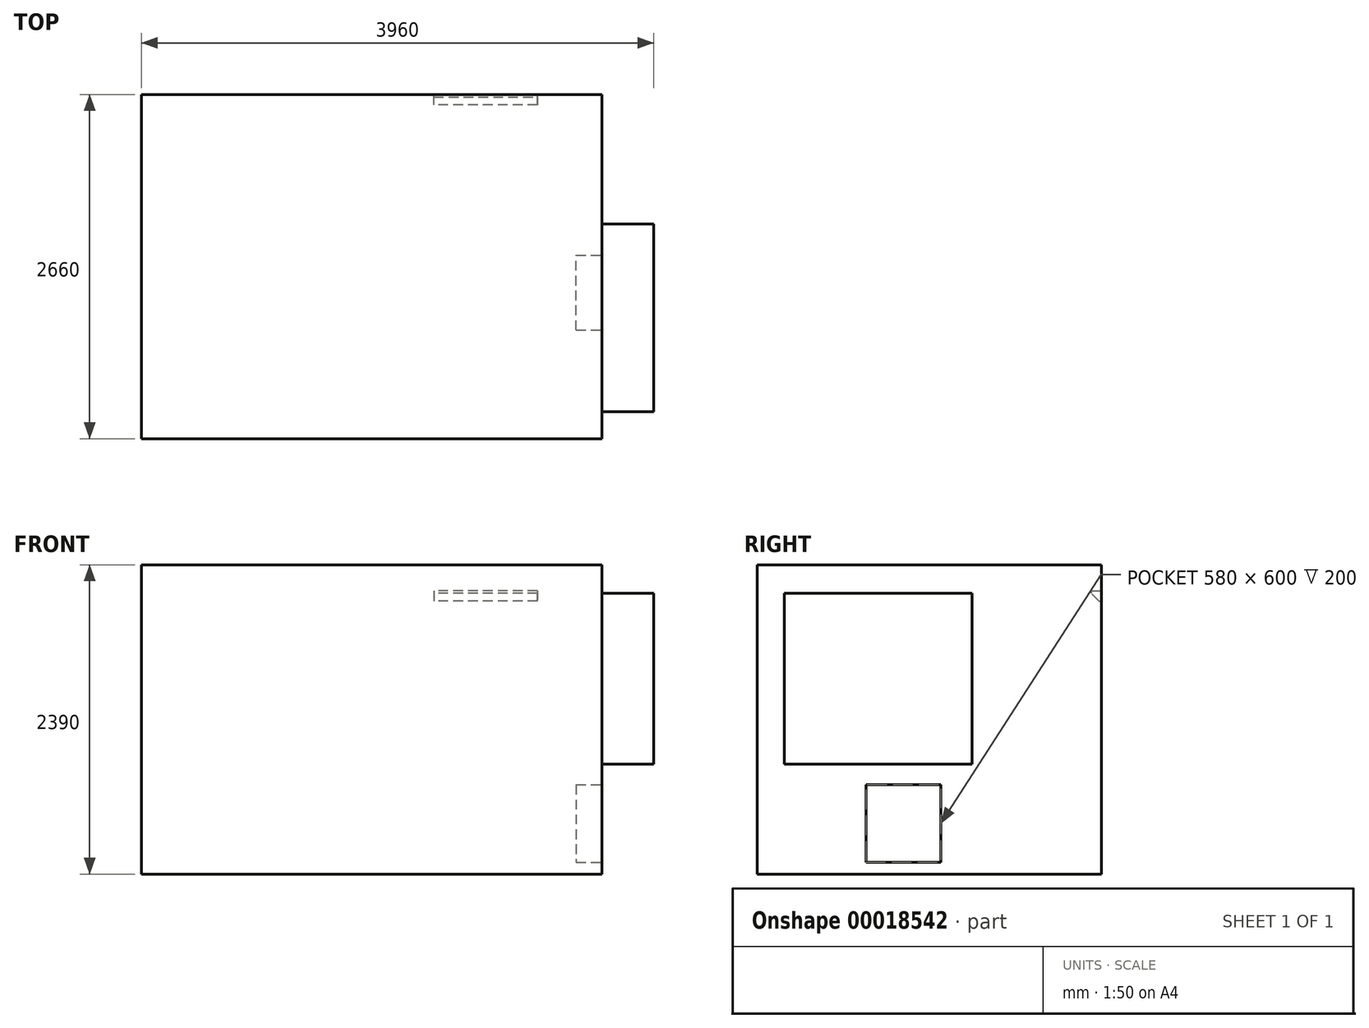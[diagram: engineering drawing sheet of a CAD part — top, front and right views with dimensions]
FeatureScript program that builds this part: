
annotation { "Feature Type Name" : "Feature", "Feature Type Description" : "" }
export const myFeature = defineFeature(function(context is Context, id is Id, definition is map)
    precondition{}
    {
        {
            var Q0;
            Q0=qCreatedBy(makeId("Right.planeOp"),FACE);
            var sketch = newSketch(context, id + "F0", { "sketchPlane" : qUnion([Q0])});
            skLineSegment(sketch, "E0", {"start": v(-1889.77, -1378.55) * mm, "end": v(770.23, -1378.55) * mm});
            skLineSegment(sketch, "E1", {"start": v(770.23, -1378.55) * mm, "end": v(770.23, 1011.45) * mm});
            skLineSegment(sketch, "E2", {"start": v(770.23, 1011.45) * mm, "end": v(-1889.77, 1011.45) * mm});
            skLineSegment(sketch, "E3", {"start": v(-1889.77, 1011.45) * mm, "end": v(-1889.77, -1378.55) * mm});
            skSolve(sketch);
        }
        {
            var Q0;
            Q0=makeQuery(id+"F0.imprint","IMPRINT",FACE,{"disambiguationData":[TD([[makeQuery(id+"F0.imprint","IMPRINT",EDGE,{"derivedFrom":sQuery(id+"F0.wireOp",EDGE,"E0")}),1.0]])]});
            extrude(context, id + "F1", {"entities" : qUnion([Q0]), "depth" : 3560 * mm});
        }
        {
            var Q0;
            Q0=makeQuery(id+"F1.opExtrude","CAP_FACE",FACE,{"disambiguationData":[OSD([sQuery(id+"F0.wireOp",EDGE,"E0"),sQuery(id+"F0.wireOp",EDGE,"E1"),sQuery(id+"F0.wireOp",EDGE,"E2"),sQuery(id+"F0.wireOp",EDGE,"E3")])],"isStart":false});
            var sketch = newSketch(context, id + "F2", { "sketchPlane" : qUnion([Q0])});
            skSolve(sketch);
        }
        {
            var Q0;
            Q0=makeQuery(id+"F2.imprint","IMPRINT",FACE,{"disambiguationData":[TD([[makeQuery(id+"F2.imprint","IMPRINT",EDGE,{"derivedFrom":makeQuery(id+"F1.opExtrude","CAP_EDGE",EDGE,{"disambiguationData":[OSD([sQuery(id+"F0.wireOp",EDGE,"E0")])],"isStart":false})}),1.0]])]});
            var sketch = newSketch(context, id + "F3", { "sketchPlane" : qUnion([Q0])});
            skLineSegment(sketch, "E4.bottom", {"start": v(-1679.77, 791.45) * mm, "end": v(-229.77, 791.45) * mm});
            skLineSegment(sketch, "E4.top", {"start": v(-1679.77, -528.55) * mm, "end": v(-229.77, -528.55) * mm});
            skLineSegment(sketch, "E4.left", {"start": v(-1679.77, 791.45) * mm, "end": v(-1679.77, -528.55) * mm});
            skLineSegment(sketch, "E4.right", {"start": v(-229.77, 791.45) * mm, "end": v(-229.77, -528.55) * mm});
            skSolve(sketch);
        }
        {
            var Q0;
            Q0=makeQuery(id+"F3.imprint","IMPRINT",FACE,{"disambiguationData":[TD([[makeQuery(id+"F3.imprint","IMPRINT",EDGE,{"derivedFrom":sQuery(id+"F3.wireOp",EDGE,"E4.bottom")}),-1.0]])]});
            extrude(context, id + "F4", {"entities" : qUnion([Q0]), "operationType" : NewBodyOperationType.ADD, "depth" : 400 * mm});
        }
        {
            var Q0;
            Q0=makeQuery(id+"F2.imprint","IMPRINT",FACE,{"disambiguationData":[TD([[makeQuery(id+"F2.imprint","IMPRINT",EDGE,{"derivedFrom":makeQuery(id+"F1.opExtrude","CAP_EDGE",EDGE,{"disambiguationData":[OSD([sQuery(id+"F0.wireOp",EDGE,"E0")])],"isStart":false})}),1.0]])]});
            var sketch = newSketch(context, id + "F5", { "sketchPlane" : qUnion([Q0])});
            skLineSegment(sketch, "E5.bottom", {"start": v(-1049.77, -688.55) * mm, "end": v(-469.77, -688.55) * mm});
            skLineSegment(sketch, "E5.top", {"start": v(-1049.77, -1288.55) * mm, "end": v(-469.77, -1288.55) * mm});
            skLineSegment(sketch, "E5.left", {"start": v(-1049.77, -688.55) * mm, "end": v(-1049.77, -1288.55) * mm});
            skLineSegment(sketch, "E5.right", {"start": v(-469.77, -688.55) * mm, "end": v(-469.77, -1288.55) * mm});
            skSolve(sketch);
        }
        {
            var Q0;
            Q0=makeQuery(id+"F5.imprint","IMPRINT",FACE,{"disambiguationData":[TD([[makeQuery(id+"F5.imprint","IMPRINT",EDGE,{"derivedFrom":sQuery(id+"F5.wireOp",EDGE,"E5.bottom")}),-1.0]])]});
            extrude(context, id + "F6", {"entities" : qUnion([Q0]), "operationType" : NewBodyOperationType.REMOVE, "oppositeDirection" : true, "depth" : 200 * mm});
        }
        {
            var Q0;
            Q0=makeQuery(id+"F1.opExtrude","SWEPT_FACE",FACE,{"disambiguationData":[OSD([sQuery(id+"F0.wireOp",EDGE,"E1")])]});
            var sketch = newSketch(context, id + "F7", { "sketchPlane" : qUnion([Q0])});
            skLineSegment(sketch, "E6.bottom", {"start": v(-3060, 811.45) * mm, "end": v(-2260, 811.45) * mm});
            skLineSegment(sketch, "E6.top", {"start": v(-3060, 731.45) * mm, "end": v(-2260, 731.45) * mm});
            skLineSegment(sketch, "E6.left", {"start": v(-3060, 811.45) * mm, "end": v(-3060, 731.45) * mm});
            skLineSegment(sketch, "E6.right", {"start": v(-2260, 811.45) * mm, "end": v(-2260, 731.45) * mm});
            skSolve(sketch);
        }
        {
            var Q0;
            Q0=makeQuery(id+"F7.imprint","IMPRINT",FACE,{"disambiguationData":[TD([[makeQuery(id+"F7.imprint","IMPRINT",EDGE,{"derivedFrom":sQuery(id+"F7.wireOp",EDGE,"E6.bottom")}),-1.0]])]});
            extrude(context, id + "F8", {"entities" : qUnion([Q0]), "operationType" : NewBodyOperationType.REMOVE, "oppositeDirection" : true, "depth" : 80 * mm});
        }
        {
            var Q0;
            Q0=makeQuery(id+"F8.boolean.opBoolean","COPY",EDGE,{"derivedFrom":makeQuery(id+"F8.opExtrude","CAP_EDGE",EDGE,{"disambiguationData":[OSD([sQuery(id+"F7.wireOp",EDGE,"E6.top")])],"isStart":false})});
            chamfer(context, id + "F9", {"entities" : qUnion([Q0]), "width" : 60 * mm, "tangentPropagation" : true});
        }
    });
